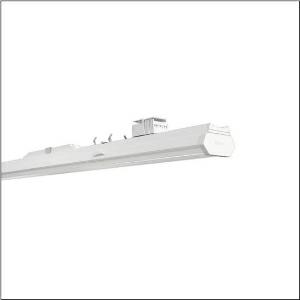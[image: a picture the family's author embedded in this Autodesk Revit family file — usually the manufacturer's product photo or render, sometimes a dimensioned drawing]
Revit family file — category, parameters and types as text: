
# Revit family: licross_r__11_protected_mo_51tp11cn49xg_312d
name_source: partatom
category: Lighting Fixtures
units: mm (PartAtom-declared; Revit-internal decimal feet)

## family parameters
Cut with Voids When Loaded = No
Host = Face
Light Source = No
Part Type = Normal
Room Calculation Point = No
Round Connector Dimension = Use Diameter
Shared = No

## types (1)
- --- (1 x LED, 9030 lm, 49.4 W, 4000K)
    Apparent Load = 49 VA
    CIE Flux Codes = 83 94 98 100 100
    Color Rendering = 80
    Color Temperature = 4000K
    Default Elevation = 1800 mm
    Description = Licross® 11 Protected MO, luminaire insert, of sheet steel, galvanised, coil coated, white, length: 1.500mm, width: 90mm, height: 101mm, LED rated luminous flux: 9.030lm, light colour: 840, control gear: ON/OFF Multilumen, CLOi, with plug, 3-pole, with phase selection, mains connection: 220..240V, AC, 50/60Hz, halogen-free wiring, primary light control with lens, of plastic, primary optical cover: cover, of PMMA, light emission: direct with ceiling illumination distribution, primary light characteristic: symmetric, protection rating (complete): IP64, insulation class (complete): insulation class I (protective earthing), certification: CE, ENEC, VDE, UKCA, protection symbol: D if used in an environment with conductive dust loads with corresponding accessories, impact resistance: IK06, permissible ambient temperature for indoor applications: -35..+40°C, corresponds to IFS (International Featured Standards) requirements for safety and quality in the food industry, reducing of maximum allowable ambient temperature of 5°C with ceiling mounting, LABS conformity tested according to VDMA 24364:2018-05, packaging unit: 1 piece
    Height = 92 mm
    Lamp = 1 x LED
    Lamp Light Flux = 9030 lm
    Lamp Power = 49.4 W
    Lamp count = 1
    Length = 1500 mm
    Luminous efficacy = 183 lm/W
    Manufacturer = Siteco
    ModVariant = No
    Model = 51TP11CN49XG
    Mounting Place = Ceiling
    Mounting Type = Pendant
    Number of Poles = 1
    OnlyDefault = Yes
    Power Factor = 1
    Product Name = Licross® 11 Protected MO
    Product group = luminaire insert
    ProductGroupID = 902
    Protection Class = Protection class I
    Protection Degree = IP 64
    RLX_Detail_Level = 1
    RlxData = <blob elided: 21789 chars, md5=596f604d>
    Socket = socket
    Standby Power = 0 W
    System Light Flux = 9030 lm
    System Power = 49 W
    Type Comments = factory setting: luminous flux: 100 % | (A | C | E) | 113 mA
    Type Image = l_1256148.jpg
    URL = http://relux.com
    VarID = @adj_003687
    Voltage = 0 V
    Weight = 0.00 kg
    Width = 88 mm

## geometry (parser evidence)
native form markers: Blend x4, Sweep x13
no freeform markers — native parametric forms only
